# Revit family: Wood_Frame_CB-52_BIM
name_source: partatom
category: Arredi
units: mm (PartAtom-declared; Revit-internal decimal feet)

## family parameters
Attiva taglio nelle viste = No
Basato su piano di lavoro = No
Condiviso = No
Numero OmniClass = 23.40.20.00
Origine composizione di rendering = Geometria famiglia
Punto di calcolo locali = No
Sempre verticale = Sì
Taglio con vuoti quando caricato = No
Titolo OmniClass = General Furniture and Specialties

## types (1)
- CB-52
    AVAILABLE FINISHES = Ebonized black lacquer on Ash (EB) or bleached, white pigment, matte acrylic on Ash (BL). Raw effect lacquer on Oak (RE). Hand rubbed natural oil on Oak or Walnut (NA), or hand rubbed black oil on Walnut (BO).
    BASE MATERIAL = BASSAM_FELLOWS_COMFORT_LEATHER_43632_CAMEL
    BIM BADGE = https://bim.archiproducts.com
    COLLECTION = Wood Frame
    DEPTH = 850 mm
    Descrizione = Low back wood and upoholstered sofa
    FEET MATERIAL = BASSAM_FELLOWS_WALNUT_BLACK_OIL_W-BO
    HEIGHT = 724 mm  [stored 2.37533 ft]
    MATERIAL DESCRIPTION = Carved, solid wood frame.‎ Upholstery in variable density foam surrounded by feather and down. Leather lacing details.
    Modello = Wood Frame Low Back Settee
    PRODUCT CODE = CB-52
    PRODUCT SHEET = https://www.archiproducts.com
    Produttore = BassamFellows
    Prospetto di default = 0 mm  [stored 0 ft]
    TECHNICAL SHEET = https://bassamfellows.com
    UPHOLSTERY MATERIAL = BASSAM_FELLOWS_COMFORT_LEATHER_43632_CAMEL
    URL = https://bassamfellows.com
    WIDTH = 1410 mm

note: [stored X ft] marks values corroborated as IEEE doubles in the binary element streams (Revit-internal decimal feet)

## geometry (parser evidence)
native form markers: Sweep x4
no freeform markers — native parametric forms only
